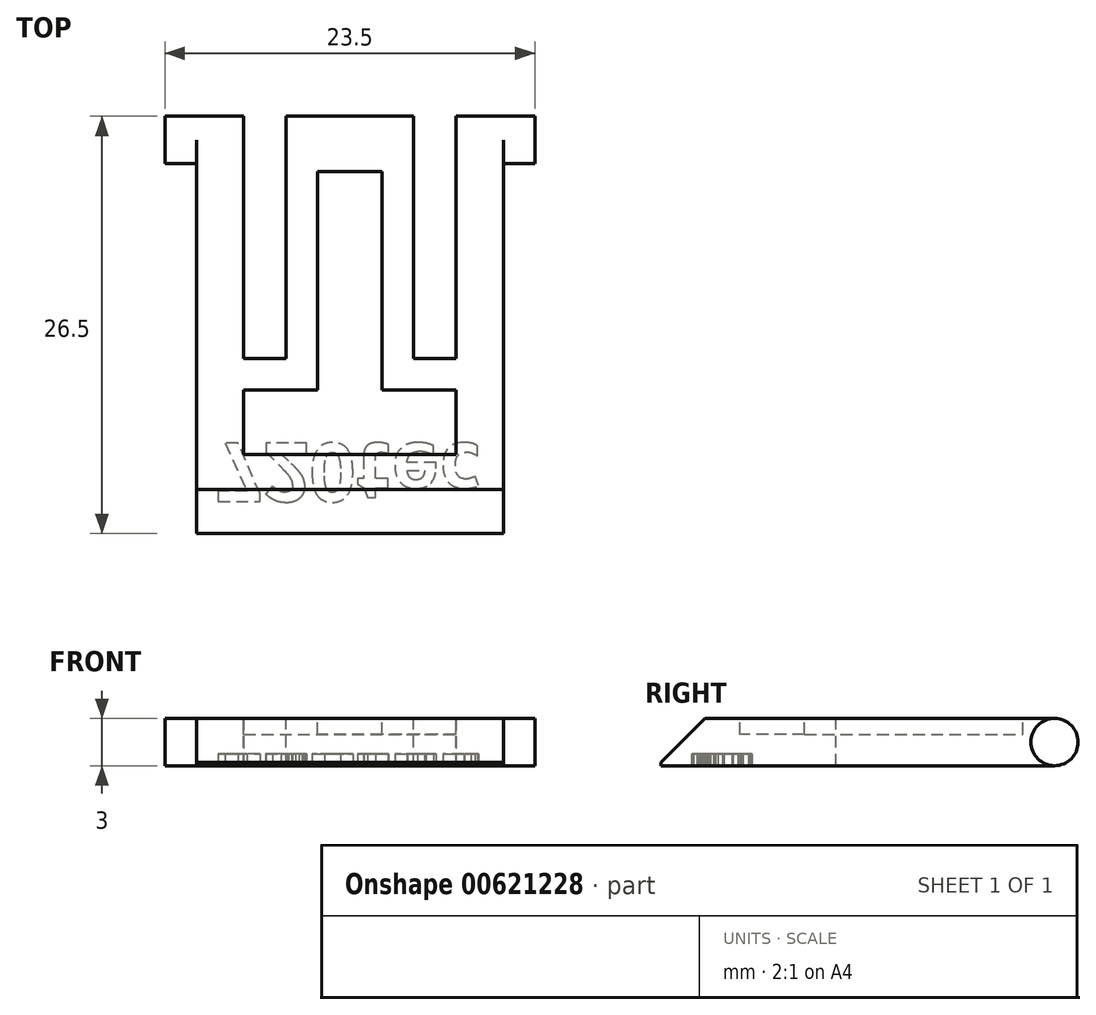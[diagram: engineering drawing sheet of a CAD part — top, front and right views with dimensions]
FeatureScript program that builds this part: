
annotation { "Feature Type Name" : "Feature", "Feature Type Description" : "" }
export const myFeature = defineFeature(function(context is Context, id is Id, definition is map)
    precondition{}
    {
        {
            var Q0;
            Q0=qCreatedBy(makeId("Top.planeOp"),FACE);
            var sketch = newSketch(context, id + "F0", { "sketchPlane" : qUnion([Q0])});
            skLineSegment(sketch, "E0.bottom", {"start": v(9.75, 13.25) * mm, "end": v(-9.75, 13.25) * mm});
            skLineSegment(sketch, "E0.top", {"start": v(9.75, -13.25) * mm, "end": v(-9.75, -13.25) * mm});
            skLineSegment(sketch, "E0.left", {"start": v(9.75, 13.25) * mm, "end": v(9.75, -13.25) * mm});
            skLineSegment(sketch, "E0.right", {"start": v(-9.75, 13.25) * mm, "end": v(-9.75, -13.25) * mm});
            skPoint(sketch, "E0.middle", {"position": v(0, 0) * mm});
            skSolve(sketch);
        }
        {
            var Q0;
            Q0 = qSketchRegion(id + "F0", true);
            extrude(context, id + "F1", {"entities" : qUnion([Q0]), "depth" : 3 * mm, "offsetDistance" : 25 * mm});
        }
        {
            var Q0;
            Q0=makeQuery(id+"F1.opExtrude","SWEPT_FACE",FACE,{"disambiguationData":[OSD([sQuery(id+"F0.wireOp",EDGE,"E0.right")])]});
            var sketch = newSketch(context, id + "F2", { "sketchPlane" : qUnion([Q0])});
            skLineSegment(sketch, "E1", {"start": v(-11.75, 3) * mm, "end": v(-11.75, 0) * mm, "construction": true});
            skLineSegment(sketch, "E2", {"start": v(-13.25, 0) * mm, "end": v(-10.25, 0) * mm});
            skLineSegment(sketch, "E3", {"start": v(-13.25, 3) * mm, "end": v(-10.25, 3) * mm});
            skLineSegment(sketch, "E4", {"start": v(-13.25, 0) * mm, "end": v(-13.25, 3) * mm});
            skLineSegment(sketch, "E5", {"start": v(-10.25, 0) * mm, "end": v(-10.25, 3) * mm});
            skSolve(sketch);
        }
        {
            var Q0;
            Q0 = qSketchRegion(id + "F2", true);
            extrude(context, id + "F3", {"entities" : qUnion([Q0]), "operationType" : NewBodyOperationType.ADD, "depth" : 2 * mm, "offsetDistance" : 25 * mm, "hasSecondDirection" : true, "secondDirectionOppositeDirection" : true, "secondDirectionDepth" : 21.5 * mm});
        }
        {
            var Q0;
            {var subQ0=sQuery(id+"F2.wireOp",EDGE,"E3");var subQ1=sQuery(id+"F2.wireOp",EDGE,"E5");var subQ2=sQuery(id+"F0.wireOp",EDGE,"E0.right");Q0=makeQuery(id+"F3.boolean.opBoolean","SPLIT",EDGE,{"disambiguationData":[TD([makeQuery(id+"F1.opExtrude","SWEPT_FACE",FACE,{"disambiguationData":[OSD([subQ2])]})])],"derivedFrom":makeQuery(id+"F3.opExtrude","SWEPT_EDGE",EDGE,{"disambiguationData":[OSD([subQ2,subQ0,subQ1])]})});}
            var Q1;
            {var subQ0=sQuery(id+"F2.wireOp",EDGE,"E2");var subQ1=sQuery(id+"F0.wireOp",EDGE,"E0.right");var subQ2=sQuery(id+"F2.wireOp",EDGE,"E5");Q1=makeQuery(id+"F3.boolean.opBoolean","SPLIT",EDGE,{"disambiguationData":[TD([makeQuery(id+"F1.opExtrude","SWEPT_FACE",FACE,{"disambiguationData":[OSD([subQ1])]})])],"derivedFrom":makeQuery(id+"F3.opExtrude","SWEPT_EDGE",EDGE,{"disambiguationData":[OSD([subQ1,subQ0,subQ2])]})});}
            var Q2;
            Q2=makeQuery(id+"F3.boolean.opBoolean","MERGE",EDGE,{"derivedFrom":[makeQuery(id+"F1.opExtrude","CAP_EDGE",EDGE,{"disambiguationData":[OSD([sQuery(id+"F0.wireOp",EDGE,"E0.bottom")])],"isStart":true}),makeQuery(id+"F3.opExtrude","SWEPT_EDGE",EDGE,{"disambiguationData":[OSD([sQuery(id+"F2.wireOp",EDGE,"E2"),sQuery(id+"F2.wireOp",EDGE,"E4")])]})]});
            var Q3;
            Q3=makeQuery(id+"F3.boolean.opBoolean","MERGE",EDGE,{"derivedFrom":[makeQuery(id+"F1.opExtrude","CAP_EDGE",EDGE,{"disambiguationData":[OSD([sQuery(id+"F0.wireOp",EDGE,"E0.bottom")])],"isStart":false}),makeQuery(id+"F3.opExtrude","SWEPT_EDGE",EDGE,{"disambiguationData":[OSD([sQuery(id+"F2.wireOp",EDGE,"E3"),sQuery(id+"F2.wireOp",EDGE,"E4")])]})]});
            var Q4;
            {var subQ0=sQuery(id+"F2.wireOp",EDGE,"E3");var subQ1=sQuery(id+"F0.wireOp",EDGE,"E0.left");var subQ2=sQuery(id+"F2.wireOp",EDGE,"E5");var subQ3=sQuery(id+"F0.wireOp",EDGE,"E0.right");Q4=makeQuery(id+"F3.boolean.opBoolean","SPLIT",EDGE,{"disambiguationData":[TD([makeQuery(id+"F1.opExtrude","SWEPT_FACE",FACE,{"disambiguationData":[OSD([subQ1])]})])],"derivedFrom":makeQuery(id+"F3.opExtrude","SWEPT_EDGE",EDGE,{"disambiguationData":[OSD([subQ3,subQ0,subQ2])]})});}
            var Q5;
            {var subQ0=sQuery(id+"F2.wireOp",EDGE,"E2");var subQ1=sQuery(id+"F0.wireOp",EDGE,"E0.right");var subQ2=sQuery(id+"F0.wireOp",EDGE,"E0.left");var subQ3=sQuery(id+"F2.wireOp",EDGE,"E5");Q5=makeQuery(id+"F3.boolean.opBoolean","SPLIT",EDGE,{"disambiguationData":[TD([makeQuery(id+"F1.opExtrude","SWEPT_FACE",FACE,{"disambiguationData":[OSD([subQ2])]})])],"derivedFrom":makeQuery(id+"F3.opExtrude","SWEPT_EDGE",EDGE,{"disambiguationData":[OSD([subQ1,subQ0,subQ3])]})});}
            fillet(context, id + "F4", {"entities" : qUnion([Q0, Q1, Q2, Q3, Q4, Q5]), "radius" : 1.5 * mm, "tangentPropagation" : true, "allowEdgeOverflow" : false});
        }
        {
            var Q0;
            Q0=makeQuery(id+"F3.boolean.opBoolean","MERGE",FACE,{"derivedFrom":[makeQuery(id+"F1.opExtrude","CAP_FACE",FACE,{"disambiguationData":[OSD([sQuery(id+"F0.wireOp",EDGE,"E0.bottom"),sQuery(id+"F0.wireOp",EDGE,"E0.top"),sQuery(id+"F0.wireOp",EDGE,"E0.left"),sQuery(id+"F0.wireOp",EDGE,"E0.right")])],"isStart":false}),makeQuery(id+"F3.opExtrude","SWEPT_FACE",FACE,{"disambiguationData":[OSD([sQuery(id+"F2.wireOp",EDGE,"E3")])]})]});
            var sketch = newSketch(context, id + "F5", { "sketchPlane" : qUnion([Q0])});
            skLineSegment(sketch, "E6", {"start": v(-9.75, 11.75) * mm, "end": v(-9.75, 18.87) * mm, "construction": true});
            skLineSegment(sketch, "E7", {"start": v(-9.75, 18.87) * mm, "end": v(-6.75, 18.87) * mm, "construction": true});
            skLineSegment(sketch, "E8", {"start": v(-6.75, 18.87) * mm, "end": v(-4.05, 18.87) * mm});
            skLineSegment(sketch, "E9", {"start": v(-4.05, 18.87) * mm, "end": v(3.95, 18.87) * mm, "construction": true});
            skLineSegment(sketch, "E10", {"start": v(-6.75, 18.87) * mm, "end": v(-6.75, -2.13) * mm});
            skLineSegment(sketch, "E11", {"start": v(-6.75, -2.13) * mm, "end": v(-4.05, -2.13) * mm});
            skLineSegment(sketch, "E12", {"start": v(-4.05, -2.13) * mm, "end": v(-4.05, 18.87) * mm});
            skLineSegment(sketch, "E13.MirrorCS", {"start": v(9.75, 11.75) * mm, "end": v(9.75, 18.87) * mm, "construction": true});
            skLineSegment(sketch, "E14.MirrorCS", {"start": v(9.75, 18.87) * mm, "end": v(6.75, 18.87) * mm, "construction": true});
            skLineSegment(sketch, "E15.MirrorCS", {"start": v(6.75, 18.87) * mm, "end": v(4.05, 18.87) * mm});
            skLineSegment(sketch, "E16.MirrorCS", {"start": v(6.75, -2.13) * mm, "end": v(4.05, -2.13) * mm});
            skLineSegment(sketch, "E17.MirrorCS", {"start": v(4.05, -2.13) * mm, "end": v(4.05, 18.87) * mm});
            skLineSegment(sketch, "E18.MirrorCS", {"start": v(6.75, 18.87) * mm, "end": v(6.75, -2.13) * mm});
            skSolve(sketch);
        }
        {
            var Q0;
            {var subQ0=sQuery(id+"F5.wireOp",EDGE,"E8");Q0=makeQuery(id+"F5.imprint","IMPRINT",FACE,{"disambiguationData":[TD([[makeQuery(id+"F5.imprint","IMPRINT",EDGE,{"derivedFrom":subQ0}),-1.0]])]});}
            var Q1;
            {var subQ0=sQuery(id+"F5.wireOp",EDGE,"E11");Q1=makeQuery(id+"F5.imprint","IMPRINT",FACE,{"disambiguationData":[TD([[makeQuery(id+"F5.imprint","IMPRINT",EDGE,{"derivedFrom":subQ0}),1.0]])]});}
            var Q2;
            {var subQ0=sQuery(id+"F5.wireOp",EDGE,"E15.MirrorCS");Q2=makeQuery(id+"F5.imprint","IMPRINT",FACE,{"disambiguationData":[TD([[makeQuery(id+"F5.imprint","IMPRINT",EDGE,{"derivedFrom":subQ0}),1.0]])]});}
            var Q3;
            {var subQ0=sQuery(id+"F5.wireOp",EDGE,"E16.MirrorCS");Q3=makeQuery(id+"F5.imprint","IMPRINT",FACE,{"disambiguationData":[TD([[makeQuery(id+"F5.imprint","IMPRINT",EDGE,{"derivedFrom":subQ0}),-1.0]])]});}
            var Q4;
            Q4=makeQuery(id+"F3.boolean.opBoolean","MERGE",FACE,{"derivedFrom":[makeQuery(id+"F1.opExtrude","CAP_FACE",FACE,{"disambiguationData":[OSD([sQuery(id+"F0.wireOp",EDGE,"E0.bottom"),sQuery(id+"F0.wireOp",EDGE,"E0.top"),sQuery(id+"F0.wireOp",EDGE,"E0.left"),sQuery(id+"F0.wireOp",EDGE,"E0.right")])],"isStart":true}),makeQuery(id+"F3.opExtrude","SWEPT_FACE",FACE,{"disambiguationData":[OSD([sQuery(id+"F2.wireOp",EDGE,"E2")])]})]});
            extrude(context, id + "F6", {"entities" : qUnion([Q0, Q1, Q2, Q3]), "operationType" : NewBodyOperationType.REMOVE, "endBound" : BoundingType.UP_TO_SURFACE, "oppositeDirection" : true, "depth" : 25 * mm, "endBoundEntityFace" : qUnion([Q4]), "offsetDistance" : 25 * mm});
        }
        {
            var Q0;
            Q0=makeQuery(id+"F1.opExtrude","CAP_EDGE",EDGE,{"disambiguationData":[OSD([sQuery(id+"F0.wireOp",EDGE,"E0.top")])],"isStart":false});
            chamfer(context, id + "F7", {"entities" : qUnion([Q0]), "width" : 2.8 * mm, "tangentPropagation" : true});
        }
        {
            var Q0;
            Q0=makeQuery(id+"F3.boolean.opBoolean","MERGE",FACE,{"derivedFrom":[makeQuery(id+"F1.opExtrude","CAP_FACE",FACE,{"disambiguationData":[OSD([sQuery(id+"F0.wireOp",EDGE,"E0.bottom"),sQuery(id+"F0.wireOp",EDGE,"E0.top"),sQuery(id+"F0.wireOp",EDGE,"E0.left"),sQuery(id+"F0.wireOp",EDGE,"E0.right")])],"isStart":true}),makeQuery(id+"F3.opExtrude","SWEPT_FACE",FACE,{"disambiguationData":[OSD([sQuery(id+"F2.wireOp",EDGE,"E2")])]})]});
            var sketch = newSketch(context, id + "F8", { "sketchPlane" : qUnion([Q0])});
            skText(sketch, "E19", { "text": "720tec", "fontName": "OpenSans-Bold.ttf"});
            const initialGuessF8  = {"E19": [-0.0085, 0.00752, 1, 0, 0.00373]};
            skSetInitialGuess(sketch, initialGuessF8);
            skSolve(sketch);
        }
        {
            var Q0;
            Q0 = qSketchRegion(id + "F8", true);
            extrude(context, id + "F9", {"entities" : qUnion([Q0]), "operationType" : NewBodyOperationType.REMOVE, "flatOperationType" : FlatOperationType.REMOVE, "oppositeDirection" : true, "depth" : 0.75 * mm, "offsetDistance" : 25 * mm, "domain" : OperationDomain.MODEL});
        }
        {
            var Q0;
            Q0=makeQuery(id+"F3.boolean.opBoolean","MERGE",FACE,{"derivedFrom":[makeQuery(id+"F1.opExtrude","CAP_FACE",FACE,{"disambiguationData":[OSD([sQuery(id+"F0.wireOp",EDGE,"E0.bottom"),sQuery(id+"F0.wireOp",EDGE,"E0.top"),sQuery(id+"F0.wireOp",EDGE,"E0.left"),sQuery(id+"F0.wireOp",EDGE,"E0.right")])],"isStart":false}),makeQuery(id+"F3.opExtrude","SWEPT_FACE",FACE,{"disambiguationData":[OSD([sQuery(id+"F2.wireOp",EDGE,"E3")])]})]});
            var sketch = newSketch(context, id + "F10", { "sketchPlane" : qUnion([Q0])});
            skLineSegment(sketch, "E20.0", {"start": v(6.75, -4.13) * mm, "end": v(2.05, -4.13) * mm});
            skLineSegment(sketch, "E20.1", {"start": v(-6.75, -4.13) * mm, "end": v(-2.05, -4.13) * mm});
            skLineSegment(sketch, "E20.2", {"start": v(-2.05, -4.13) * mm, "end": v(-2.05, 9.75) * mm});
            skLineSegment(sketch, "E20.3", {"start": v(2.05, 9.75) * mm, "end": v(-2.05, 9.75) * mm});
            skLineSegment(sketch, "E20.4", {"start": v(2.05, -4.13) * mm, "end": v(2.05, 9.75) * mm});
            skLineSegment(sketch, "E21", {"start": v(-6.75, -4.13) * mm, "end": v(-6.75, -8.24) * mm});
            skLineSegment(sketch, "E22", {"start": v(-6.75, -8.24) * mm, "end": v(6.75, -8.24) * mm});
            skLineSegment(sketch, "E23", {"start": v(6.75, -8.24) * mm, "end": v(6.75, -4.13) * mm});
            skSolve(sketch);
        }
        {
            var Q0;
            Q0=makeQuery(id+"F10.imprint","IMPRINT",FACE,{"disambiguationData":[TD([[makeQuery(id+"F10.imprint","IMPRINT",EDGE,{"derivedFrom":sQuery(id+"F10.wireOp",EDGE,"E20.0")}),1.0]])]});
            extrude(context, id + "F11", {"entities" : qUnion([Q0]), "operationType" : NewBodyOperationType.REMOVE, "oppositeDirection" : true, "depth" : 1 * mm, "offsetDistance" : 25 * mm});
        }
    });
